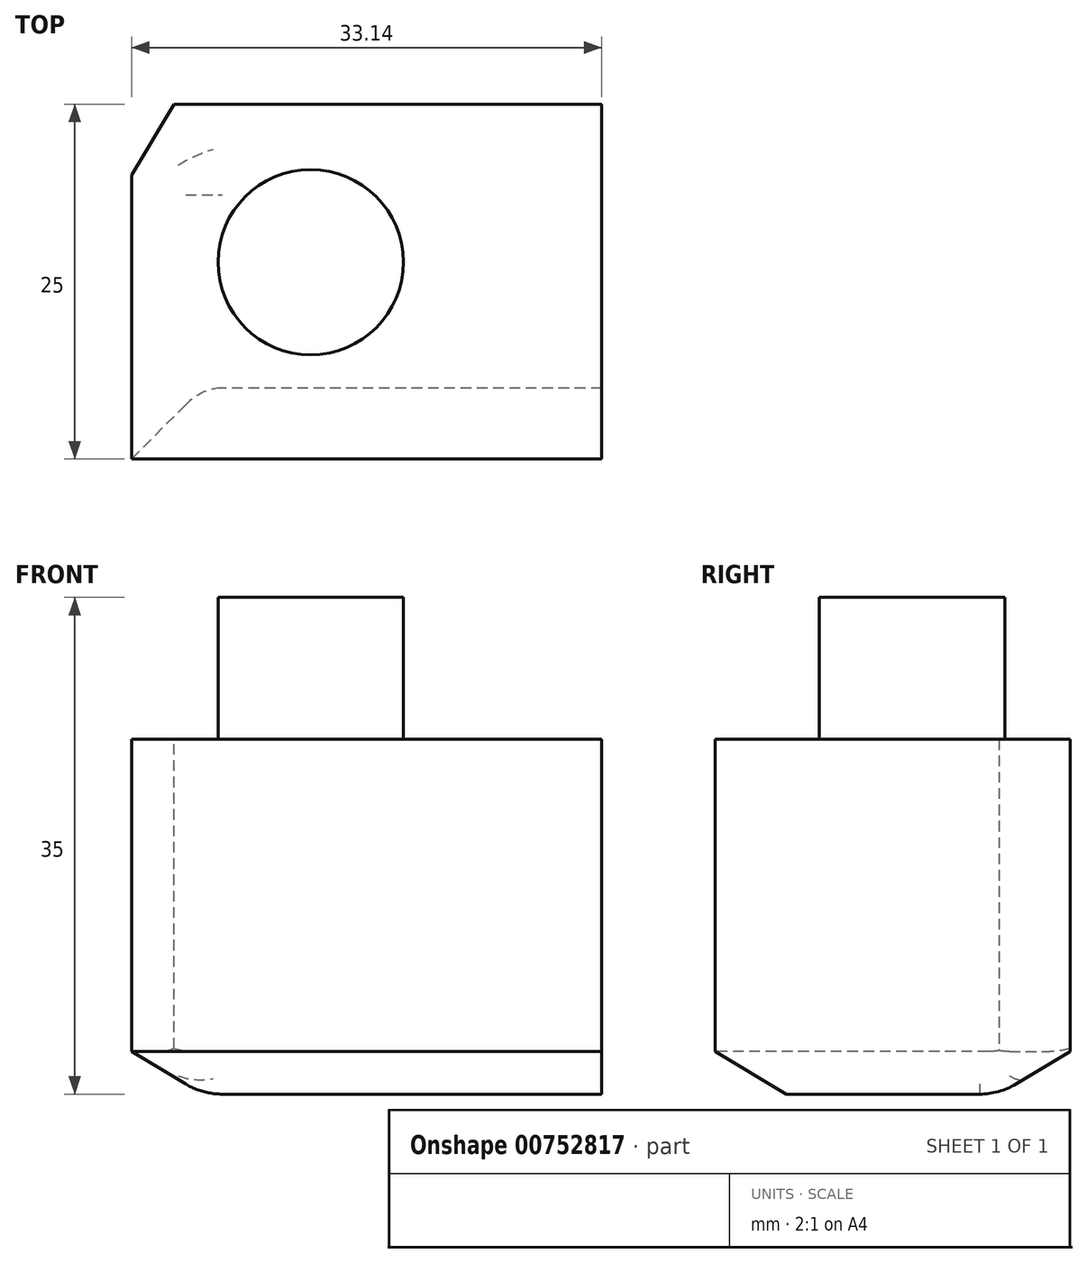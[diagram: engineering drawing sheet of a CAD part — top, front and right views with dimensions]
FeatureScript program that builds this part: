
annotation { "Feature Type Name" : "Feature", "Feature Type Description" : "" }
export const myFeature = defineFeature(function(context is Context, id is Id, definition is map)
    precondition{}
    {
        {
            var Q0;
            Q0=qCreatedBy(makeId("Front.planeOp"),FACE);
            var sketch = newSketch(context, id + "F0", { "sketchPlane" : qUnion([Q0])});
            skLineSegment(sketch, "E0.bottom", {"start": v(0, 0) * mm, "end": v(-33.14, 0) * mm});
            skLineSegment(sketch, "E0.top", {"start": v(0, 25) * mm, "end": v(-33.14, 25) * mm});
            skLineSegment(sketch, "E0.left", {"start": v(0, 0) * mm, "end": v(0, 25) * mm});
            skLineSegment(sketch, "E0.right", {"start": v(-33.14, 0) * mm, "end": v(-33.14, 25) * mm});
            skSolve(sketch);
        }
        {
            var Q0;
            Q0=makeQuery(id+"F0.imprint","IMPRINT",FACE,{"disambiguationData":[TD([[makeQuery(id+"F0.imprint","IMPRINT",EDGE,{"derivedFrom":sQuery(id+"F0.wireOp",EDGE,"E0.bottom")}),-1.0]])]});
            extrude(context, id + "F1", {"entities" : qUnion([Q0]), "depth" : 25 * mm, "offsetDistance" : 25 * mm});
        }
        {
            var Q0;
            Q0=makeQuery(id+"F1.opExtrude","CAP_EDGE",EDGE,{"disambiguationData":[OSD([sQuery(id+"F0.wireOp",EDGE,"E0.bottom")])],"isStart":true});
            var Q1;
            Q1=makeQuery(id+"F1.opExtrude","SWEPT_EDGE",EDGE,{"disambiguationData":[OSD([sQuery(id+"F0.wireOp",EDGE,"E0.bottom"),sQuery(id+"F0.wireOp",EDGE,"E0.right")])]});
            var Q2;
            Q2=makeQuery(id+"F1.opExtrude","CAP_EDGE",EDGE,{"disambiguationData":[OSD([sQuery(id+"F0.wireOp",EDGE,"E0.bottom")])],"isStart":false});
            var Q3;
            Q3=makeQuery(id+"F1.opExtrude","CAP_EDGE",EDGE,{"disambiguationData":[OSD([sQuery(id+"F0.wireOp",EDGE,"E0.right")])],"isStart":true});
            chamfer(context, id + "F2", {"entities" : qUnion([Q0, Q1, Q2, Q3]), "chamferType" : ChamferType.TWO_OFFSETS, "width1" : 3 * mm, "oppositeDirection" : false, "width2" : 5 * mm, "tangentPropagation" : true});
        }
        {
            var Q0;
            {var subQ0=sQuery(id+"F0.wireOp",EDGE,"E0.bottom");Q0=makeQuery(id+"F2.opChamfer","BLEND_EDGE",EDGE,{"blendedFrom":[makeQuery(id+"F1.opExtrude","CAP_EDGE",EDGE,{"disambiguationData":[OSD([subQ0])],"isStart":true}),makeQuery(id+"F1.opExtrude","SWEPT_FACE",FACE,{"disambiguationData":[OSD([subQ0])]})],"blendedInto":[makeQuery(id+"F1.opExtrude","SWEPT_FACE",FACE,{"disambiguationData":[OSD([subQ0])]})]});}
            var Q1;
            {var subQ0=sQuery(id+"F0.wireOp",EDGE,"E0.bottom");Q1=makeQuery(id+"F2.opChamfer","BLEND_EDGE",EDGE,{"blendedFrom":[makeQuery(id+"F1.opExtrude","CAP_VERTEX",VERTEX,{"disambiguationData":[OSD([subQ0,sQuery(id+"F0.wireOp",EDGE,"E0.right")])],"isStart":true}),makeQuery(id+"F1.opExtrude","CAP_EDGE",EDGE,{"disambiguationData":[OSD([subQ0])],"isStart":true})],"blendedInto":[]});}
            var Q2;
            {var subQ0=sQuery(id+"F0.wireOp",EDGE,"E0.right");var subQ1=sQuery(id+"F0.wireOp",EDGE,"E0.bottom");Q2=makeQuery(id+"F2.opChamfer","BLEND_EDGE",EDGE,{"blendedFrom":[makeQuery(id+"F1.opExtrude","CAP_VERTEX",VERTEX,{"disambiguationData":[OSD([subQ1,subQ0])],"isStart":true}),makeQuery(id+"F1.opExtrude","SWEPT_EDGE",EDGE,{"disambiguationData":[OSD([subQ1,subQ0])]})],"blendedInto":[]});}
            var Q3;
            {var subQ0=sQuery(id+"F0.wireOp",EDGE,"E0.bottom");Q3=makeQuery(id+"F2.opChamfer","BLEND_EDGE",EDGE,{"blendedFrom":[makeQuery(id+"F1.opExtrude","SWEPT_EDGE",EDGE,{"disambiguationData":[OSD([subQ0,sQuery(id+"F0.wireOp",EDGE,"E0.right")])]}),makeQuery(id+"F1.opExtrude","SWEPT_FACE",FACE,{"disambiguationData":[OSD([subQ0])]})],"blendedInto":[makeQuery(id+"F1.opExtrude","SWEPT_FACE",FACE,{"disambiguationData":[OSD([subQ0])]})]});}
            fillet(context, id + "F3", {"entities" : qUnion([Q0, Q1, Q2, Q3]), "radius" : 5 * mm, "tangentPropagation" : true, "allowEdgeOverflow" : false});
        }
        {
            var Q0;
            Q0=makeQuery(id+"F1.opExtrude","SWEPT_FACE",FACE,{"disambiguationData":[OSD([sQuery(id+"F0.wireOp",EDGE,"E0.top")])]});
            var sketch = newSketch(context, id + "F4", { "sketchPlane" : qUnion([Q0])});
            skCircle(sketch, "E1", {"center": v(-20.51, -11.13) * mm, "radius": 6.53 * mm});
            skSolve(sketch);
        }
        {
            var Q0;
            Q0=makeQuery(id+"F4.imprint","IMPRINT",FACE,{"disambiguationData":[TD([[makeQuery(id+"F4.imprint","IMPRINT",EDGE,{"derivedFrom":sQuery(id+"F4.wireOp",EDGE,"E1")}),1.0]])]});
            extrude(context, id + "F5", {"entities" : qUnion([Q0]), "operationType" : NewBodyOperationType.ADD, "depth" : 10 * mm, "offsetDistance" : 25 * mm});
        }
    });
